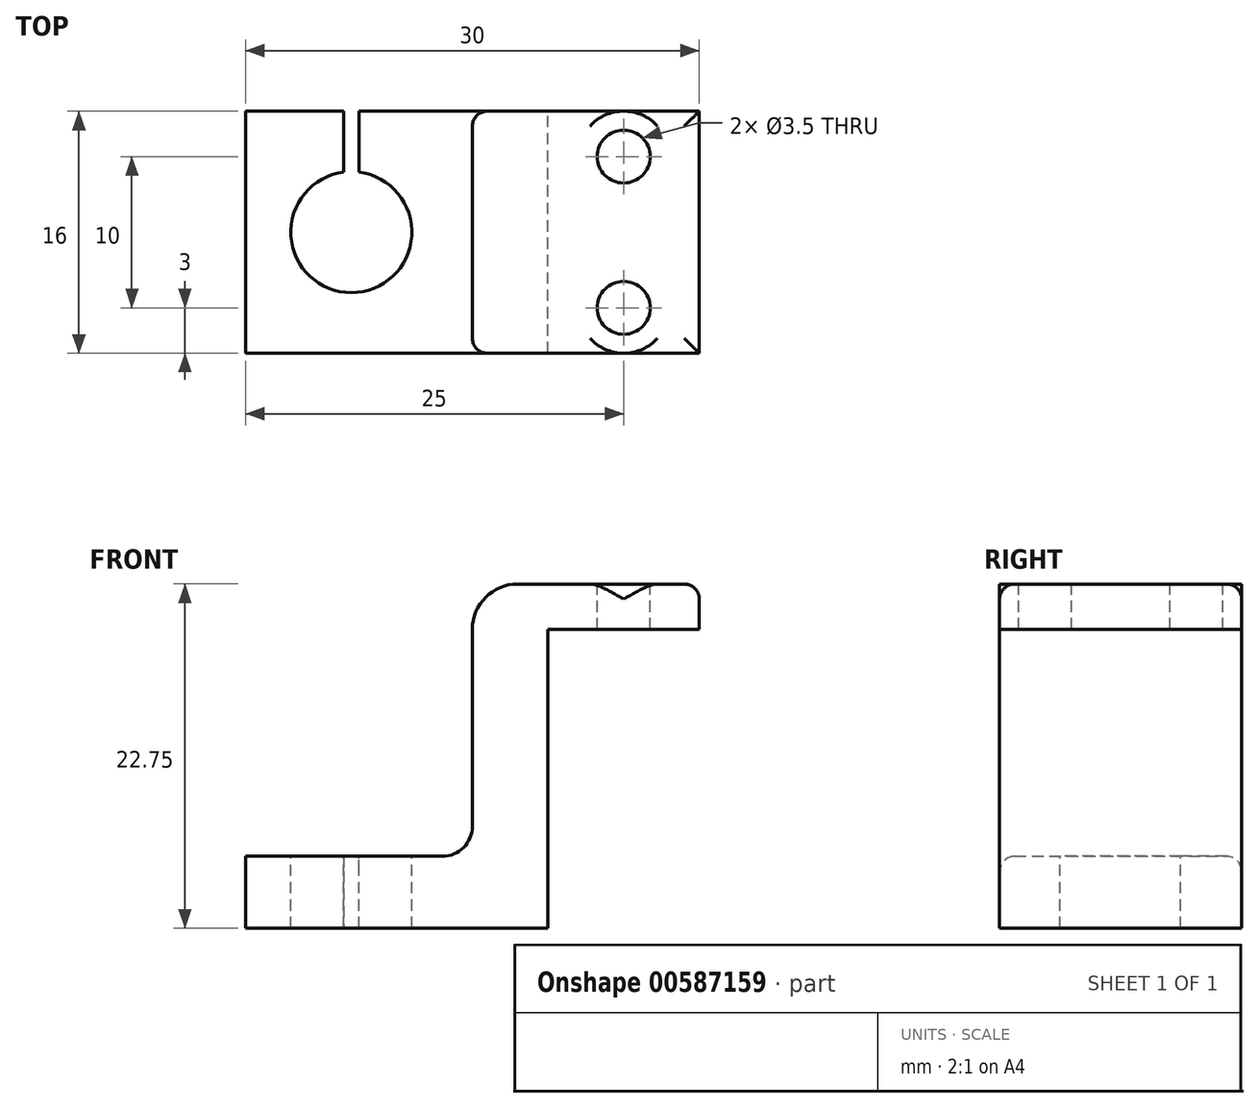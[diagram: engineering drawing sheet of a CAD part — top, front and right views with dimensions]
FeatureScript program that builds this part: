
annotation { "Feature Type Name" : "Feature", "Feature Type Description" : "" }
export const myFeature = defineFeature(function(context is Context, id is Id, definition is map)
    precondition{}
    {
        {
            var Q0;
            Q0=qCreatedBy(makeId("Front.planeOp"),FACE);
            var sketch = newSketch(context, id + "F0", { "sketchPlane" : qUnion([Q0])});
            skLineSegment(sketch, "E0", {"start": v(0, 0) * mm, "end": v(20, 0) * mm});
            skLineSegment(sketch, "E1", {"start": v(20, 0) * mm, "end": v(20, 19.75) * mm});
            skLineSegment(sketch, "E2", {"start": v(20, 19.75) * mm, "end": v(30, 19.75) * mm});
            skLineSegment(sketch, "E3", {"start": v(30, 19.75) * mm, "end": v(30, 22.75) * mm});
            skLineSegment(sketch, "E4", {"start": v(30, 22.75) * mm, "end": v(15, 22.75) * mm});
            skLineSegment(sketch, "E5", {"start": v(15, 22.75) * mm, "end": v(15, 4.75) * mm});
            skLineSegment(sketch, "E6", {"start": v(15, 4.75) * mm, "end": v(0, 4.75) * mm});
            skLineSegment(sketch, "E7", {"start": v(0, 4.75) * mm, "end": v(0, 0) * mm});
            skSolve(sketch);
        }
        {
            var Q0;
            Q0 = qSketchRegion(id + "F0", true);
            extrude(context, id + "F1", {"entities" : qUnion([Q0]), "depth" : 16 * mm, "offsetDistance" : 25 * mm});
        }
        {
            var Q0;
            Q0=makeQuery(id+"F1.opExtrude","SWEPT_FACE",FACE,{"disambiguationData":[OSD([sQuery(id+"F0.wireOp",EDGE,"E4")])]});
            var sketch = newSketch(context, id + "F2", { "sketchPlane" : qUnion([Q0])});
            skCircle(sketch, "E8", {"center": v(25, -3) * mm, "radius": 1.75 * mm});
            skCircle(sketch, "E9", {"center": v(25, -13) * mm, "radius": 1.75 * mm});
            skSolve(sketch);
        }
        {
            var Q0;
            Q0 = qSketchRegion(id + "F2", true);
            extrude(context, id + "F3", {"entities" : qUnion([Q0]), "operationType" : NewBodyOperationType.REMOVE, "oppositeDirection" : true, "depth" : 25 * mm, "offsetDistance" : 25 * mm});
        }
        {
            var Q0;
            Q0=makeQuery(id+"F1.opExtrude","SWEPT_FACE",FACE,{"disambiguationData":[OSD([sQuery(id+"F0.wireOp",EDGE,"E6")])]});
            var sketch = newSketch(context, id + "F4", { "sketchPlane" : qUnion([Q0])});
            skArc(sketch, "E10", {"start": v(3.03, -8.5) * mm, "mid": v(9.83, -10.83) * mm, "end": v(7.5, -4.03) * mm});
            skPoint(sketch, "E10.centerSnap0", {"position": v(0, -8) * mm});
            skArc(sketch, "E11", {"start": v(3.03, -7.5) * mm, "mid": v(3, -8) * mm, "end": v(3.03, -8.5) * mm});
            skLineSegment(sketch, "E12", {"start": v(7, -8) * mm, "end": v(10.9, -11.9) * mm, "construction": true});
            skLineSegment(sketch, "E13.MirrorCS", {"start": v(7.5, 0.27) * mm, "end": v(6.5, 0.27) * mm});
            skLineSegment(sketch, "E14.MirrorCS", {"start": v(6.5, 0.27) * mm, "end": v(6.5, -4.03) * mm});
            skLineSegment(sketch, "E15.MirrorCS", {"start": v(7.5, -4.03) * mm, "end": v(7.5, 0.27) * mm});
            skPoint(sketch, "E16.MirrorP", {"position": v(7, -1) * mm});
            skArc(sketch, "E17.MirrorCS", {"start": v(6.5, -4.03) * mm, "mid": v(7, -4) * mm, "end": v(7.5, -4.03) * mm});
            skArc(sketch, "E18.trimOffspring", {"start": v(6.5, -4.03) * mm, "mid": v(4.17, -5.17) * mm, "end": v(3.03, -7.5) * mm});
            skSolve(sketch);
        }
        {
            var Q0;
            Q0 = qSketchRegion(id + "F4", true);
            extrude(context, id + "F5", {"entities" : qUnion([Q0]), "operationType" : NewBodyOperationType.REMOVE, "oppositeDirection" : true, "depth" : 25 * mm, "offsetDistance" : 25 * mm});
        }
        {
            var Q0;
            Q0=makeQuery(id+"F1.opExtrude","SWEPT_EDGE",EDGE,{"disambiguationData":[OSD([sQuery(id+"F0.wireOp",EDGE,"E5"),sQuery(id+"F0.wireOp",EDGE,"E6")])]});
            fillet(context, id + "F6", {"entities" : qUnion([Q0]), "radius" : 2 * mm, "tangentPropagation" : true, "allowEdgeOverflow" : false});
        }
        {
            var Q0;
            Q0=makeQuery(id+"F1.opExtrude","SWEPT_EDGE",EDGE,{"disambiguationData":[OSD([sQuery(id+"F0.wireOp",EDGE,"E4"),sQuery(id+"F0.wireOp",EDGE,"E5")])]});
            fillet(context, id + "F7", {"entities" : qUnion([Q0]), "radius" : 3 * mm, "tangentPropagation" : true, "allowEdgeOverflow" : false});
        }
        {
            var Q0;
            Q0=makeQuery(id+"F1.opExtrude","SWEPT_EDGE",EDGE,{"disambiguationData":[OSD([sQuery(id+"F0.wireOp",EDGE,"E3"),sQuery(id+"F0.wireOp",EDGE,"E4")])]});
            var Q1;
            Q1=makeQuery(id+"F1.opExtrude","CAP_EDGE",EDGE,{"disambiguationData":[OSD([sQuery(id+"F0.wireOp",EDGE,"E4")])],"isStart":false});
            var Q2;
            Q2=makeQuery(id+"F1.opExtrude","CAP_EDGE",EDGE,{"disambiguationData":[OSD([sQuery(id+"F0.wireOp",EDGE,"E4")])],"isStart":true});
            fillet(context, id + "F8", {"entities" : qUnion([Q0, Q1, Q2]), "radius" : 1 * mm, "tangentPropagation" : true, "allowEdgeOverflow" : false});
        }
        {
            var Q0;
            Q0=makeQuery(id+"F1.opExtrude","SWEPT_FACE",FACE,{"disambiguationData":[OSD([sQuery(id+"F0.wireOp",EDGE,"E4")])]});
            var sketch = newSketch(context, id + "F9", { "sketchPlane" : qUnion([Q0])});
            skCircle(sketch, "E19", {"center": v(25, -3) * mm, "radius": 3 * mm});
            skCircle(sketch, "E20", {"center": v(25, -13) * mm, "radius": 3 * mm});
            skCircle(sketch, "E21", {"center": v(25, -3) * mm, "radius": 1.75 * mm});
            skCircle(sketch, "E22", {"center": v(25, -13) * mm, "radius": 1.75 * mm});
            skSolve(sketch);
        }
        {
            var Q0;
            Q0 = qSketchRegion(id + "F9", true);
            extrude(context, id + "F10", {"entities" : qUnion([Q0]), "operationType" : NewBodyOperationType.ADD, "oppositeDirection" : true, "depth" : 2 * mm, "offsetDistance" : 25 * mm});
        }
        {
            var Q0;
            {var subQ0=sQuery(id+"F0.wireOp",EDGE,"E7");var subQ1=sQuery(id+"F0.wireOp",EDGE,"E6");Q0=makeQuery(id+"F5.boolean.opBoolean","SPLIT",EDGE,{"disambiguationData":[TD([makeQuery(id+"F1.opExtrude","SWEPT_FACE",FACE,{"disambiguationData":[OSD([subQ0])]})])],"derivedFrom":makeQuery(id+"F1.opExtrude","CAP_EDGE",EDGE,{"disambiguationData":[OSD([subQ1])],"isStart":true})});}
            fillet(context, id + "F11", {"entities" : qUnion([Q0]), "radius" : 1 * mm, "tangentPropagation" : true, "allowEdgeOverflow" : false});
        }
    });
